# Revit family: 52042-presto
name_source: partatom
category: Plumbing Fixtures
units: mm (PartAtom-declared; Revit-internal decimal feet)

## family parameters
Always vertical = Yes
Cut with Voids When Loaded = No
Maintain Annotation Orientation = No
OmniClass Number = 23.45.00.00
OmniClass Title = Sanitary, Laundry, and Cleaning Equipment
Part Type = Normal
Room Calculation Point = No
Round Connector Dimension = Use Diameter
Shared = No
Work Plane-Based = Yes

## types (1)
- 52042- Les Robinets PRESTO
    Default Elevation = 1219 mm
    Description = Wall-mounted electronic soap dispenser with infrared sensor (self-adjusting)
Consistent with PRESTORIZON wall-mounted sensor taps
Work with peristaltic pump, allowing use of liquid soap, detergent, lotion or antibacterial gel
Soap viscosity : 100-3800 cPs
    Model = 52042-presto
    URL = https://www.prestodatashare.com
    brand = Les Robinets PRESTO
    range = PRESTORIZON - Wall-mounted sensor taps range
    ref = 52042 - Wall-mounted electronic soap dispenser

## geometry (parser evidence)
native form markers: Sweep x2
no freeform markers — native parametric forms only
